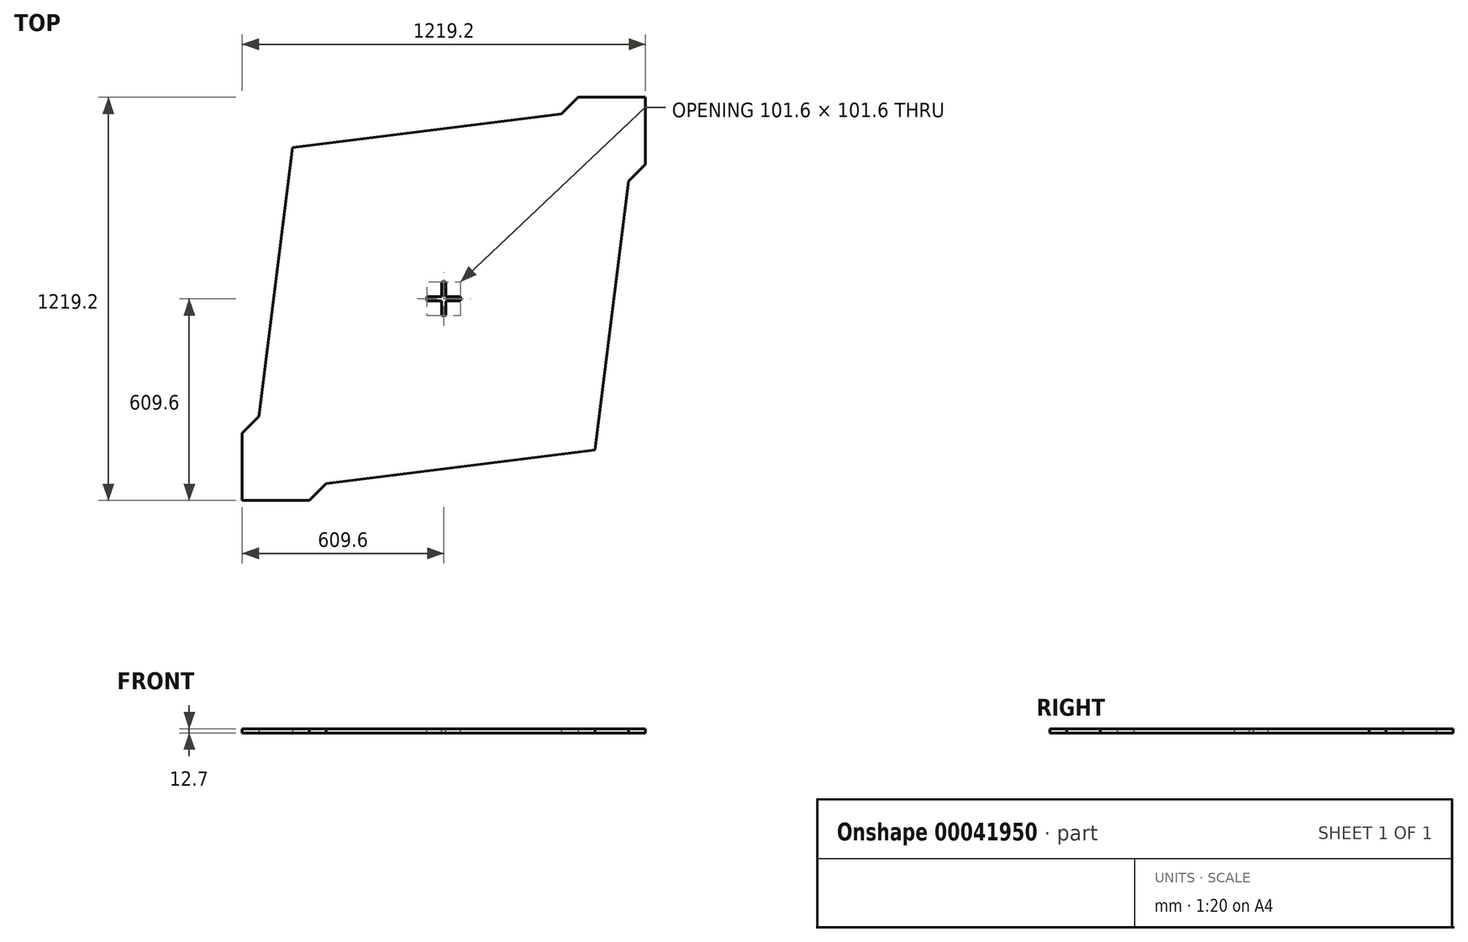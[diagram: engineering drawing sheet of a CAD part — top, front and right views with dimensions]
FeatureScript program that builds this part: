
annotation { "Feature Type Name" : "Feature", "Feature Type Description" : "" }
export const myFeature = defineFeature(function(context is Context, id is Id, definition is map)
    precondition{}
    {
        {
            var Q0;
            Q0=qCreatedBy(makeId("Top.planeOp"),FACE);
            var sketch = newSketch(context, id + "F0", { "sketchPlane" : qUnion([Q0])});
            skLineSegment(sketch, "E0.bottom", {"start": v(0, 0) * mm, "end": v(1219.2, 0) * mm});
            skLineSegment(sketch, "E0.top", {"start": v(0, 1219.2) * mm, "end": v(1219.2, 1219.2) * mm});
            skLineSegment(sketch, "E0.left", {"start": v(0, 0) * mm, "end": v(0, 1219.2) * mm});
            skLineSegment(sketch, "E0.right", {"start": v(1219.2, 0) * mm, "end": v(1219.2, 1219.2) * mm});
            skSolve(sketch);
        }
        {
            var Q0;
            Q0 = qSketchRegion(id + "F0", true);
            extrude(context, id + "F1", {"entities" : qUnion([Q0]), "depth" : 12.7 * mm});
        }
        {
            var Q0;
            Q0=makeQuery(id+"F1.opExtrude","CAP_FACE",FACE,{"disambiguationData":[OSD([sQuery(id+"F0.wireOp",EDGE,"E0.bottom"),sQuery(id+"F0.wireOp",EDGE,"E0.top"),sQuery(id+"F0.wireOp",EDGE,"E0.left"),sQuery(id+"F0.wireOp",EDGE,"E0.right")])],"isStart":true});
            var sketch = newSketch(context, id + "F2", { "sketchPlane" : qUnion([Q0])});
            skLineSegment(sketch, "E1", {"start": v(0, -203.2) * mm, "end": v(0, -1219.2) * mm});
            skLineSegment(sketch, "E2", {"start": v(0, -1219.2) * mm, "end": v(1016, -1219.2) * mm});
            skLineSegment(sketch, "E3", {"start": v(0, -203.2) * mm, "end": v(50.8, -254) * mm});
            skLineSegment(sketch, "E4", {"start": v(50.8, -254) * mm, "end": v(152.4, -1066.8) * mm});
            skLineSegment(sketch, "E5", {"start": v(152.4, -1066.8) * mm, "end": v(965.2, -1168.4) * mm});
            skLineSegment(sketch, "E6", {"start": v(1016, -1219.2) * mm, "end": v(965.2, -1168.4) * mm});
            skSolve(sketch);
        }
        {
            var Q0;
            Q0=makeQuery(id+"F2.imprint","IMPRINT",FACE,{"disambiguationData":[TD([[makeQuery(id+"F2.imprint","IMPRINT",EDGE,{"derivedFrom":sQuery(id+"F2.wireOp",EDGE,"E1")}),1.0]])]});
            extrude(context, id + "F3", {"entities" : qUnion([Q0]), "operationType" : NewBodyOperationType.REMOVE, "endBound" : BoundingType.THROUGH_ALL, "oppositeDirection" : true, "depth" : 25.4 * mm});
        }
        {
            var Q0;
            Q0=makeQuery(id+"F1.opExtrude","CAP_FACE",FACE,{"disambiguationData":[OSD([sQuery(id+"F0.wireOp",EDGE,"E0.bottom"),sQuery(id+"F0.wireOp",EDGE,"E0.top"),sQuery(id+"F0.wireOp",EDGE,"E0.left"),sQuery(id+"F0.wireOp",EDGE,"E0.right")])],"isStart":true});
            var sketch = newSketch(context, id + "F4", { "sketchPlane" : qUnion([Q0])});
            skLineSegment(sketch, "E7.MirrorCS", {"start": v(1066.8, -152.4) * mm, "end": v(1168.4, -965.2) * mm});
            skLineSegment(sketch, "E8.MirrorCS", {"start": v(254, -50.8) * mm, "end": v(1066.8, -152.4) * mm});
            skLineSegment(sketch, "E9.MirrorCS", {"start": v(1168.4, -965.2) * mm, "end": v(1219.2, -1016) * mm});
            skLineSegment(sketch, "E10.MirrorCS", {"start": v(203.2, 0) * mm, "end": v(254, -50.8) * mm});
            skLineSegment(sketch, "E11.MirrorCS", {"start": v(1219.2, 0) * mm, "end": v(203.2, 0) * mm});
            skLineSegment(sketch, "E12.MirrorCS", {"start": v(1219.2, -1016) * mm, "end": v(1219.2, 0) * mm});
            skSolve(sketch);
        }
        {
            var Q0;
            Q0 = qSketchRegion(id + "F4", true);
            extrude(context, id + "F5", {"entities" : qUnion([Q0]), "operationType" : NewBodyOperationType.REMOVE, "endBound" : BoundingType.THROUGH_ALL, "oppositeDirection" : true, "depth" : 25.4 * mm});
        }
        {
            var Q0;
            Q0=makeQuery(id+"F1.opExtrude","CAP_FACE",FACE,{"disambiguationData":[OSD([sQuery(id+"F0.wireOp",EDGE,"E0.bottom"),sQuery(id+"F0.wireOp",EDGE,"E0.top"),sQuery(id+"F0.wireOp",EDGE,"E0.left"),sQuery(id+"F0.wireOp",EDGE,"E0.right")])],"isStart":false});
            var sketch = newSketch(context, id + "F6", { "sketchPlane" : qUnion([Q0])});
            skLineSegment(sketch, "E13", {"start": v(609.6, 660.4) * mm, "end": v(609.6, 558.8) * mm});
            skLineSegment(sketch, "E14", {"start": v(558.8, 609.6) * mm, "end": v(660.4, 609.6) * mm});
            skLineSegment(sketch, "E15", {"start": v(609.6, 660.4) * mm, "end": v(615.95, 660.4) * mm});
            skLineSegment(sketch, "E16.MirrorCS", {"start": v(609.6, 660.4) * mm, "end": v(603.25, 660.4) * mm});
            skLineSegment(sketch, "E17.MirrorCS", {"start": v(609.6, 558.8) * mm, "end": v(603.25, 558.8) * mm});
            skLineSegment(sketch, "E18.MirrorCS", {"start": v(609.6, 558.8) * mm, "end": v(615.95, 558.8) * mm});
            skLineSegment(sketch, "E19", {"start": v(603.25, 660.4) * mm, "end": v(603.25, 558.8) * mm});
            skLineSegment(sketch, "E20", {"start": v(615.95, 660.4) * mm, "end": v(615.95, 558.8) * mm});
            skLineSegment(sketch, "E21", {"start": v(558.8, 609.6) * mm, "end": v(558.8, 615.95) * mm});
            skLineSegment(sketch, "E22.MirrorCS", {"start": v(660.4, 609.6) * mm, "end": v(660.4, 615.95) * mm});
            skLineSegment(sketch, "E23.MirrorCS", {"start": v(558.8, 609.6) * mm, "end": v(558.8, 603.25) * mm});
            skLineSegment(sketch, "E24.MirrorCS", {"start": v(660.4, 609.6) * mm, "end": v(660.4, 603.25) * mm});
            skLineSegment(sketch, "E25", {"start": v(558.8, 615.95) * mm, "end": v(660.4, 615.95) * mm});
            skLineSegment(sketch, "E26", {"start": v(660.4, 603.25) * mm, "end": v(558.8, 603.25) * mm});
            skSolve(sketch);
        }
        {
            var Q0;
            {var subQ3=sQuery(id+"F6.wireOp",EDGE,"E17.MirrorCS");Q0=makeQuery(id+"F6.imprint","IMPRINT",FACE,{"disambiguationData":[TD([[makeQuery(id+"F6.imprint","IMPRINT",EDGE,{"derivedFrom":subQ3}),-1.0]])]});}
            var Q1;
            {var subQ5=sQuery(id+"F6.wireOp",EDGE,"E18.MirrorCS");Q1=makeQuery(id+"F6.imprint","IMPRINT",FACE,{"disambiguationData":[TD([[makeQuery(id+"F6.imprint","IMPRINT",EDGE,{"derivedFrom":subQ5}),1.0]])]});}
            var Q2;
            {var subQ3=sQuery(id+"F6.wireOp",EDGE,"E21");Q2=makeQuery(id+"F6.imprint","IMPRINT",FACE,{"disambiguationData":[TD([[makeQuery(id+"F6.imprint","IMPRINT",EDGE,{"derivedFrom":subQ3}),-1.0]])]});}
            var Q3;
            {var subQ3=sQuery(id+"F6.wireOp",EDGE,"E23.MirrorCS");Q3=makeQuery(id+"F6.imprint","IMPRINT",FACE,{"disambiguationData":[TD([[makeQuery(id+"F6.imprint","IMPRINT",EDGE,{"derivedFrom":subQ3}),1.0]])]});}
            var Q4;
            {var subQ3=sQuery(id+"F6.wireOp",EDGE,"E22.MirrorCS");Q4=makeQuery(id+"F6.imprint","IMPRINT",FACE,{"disambiguationData":[TD([[makeQuery(id+"F6.imprint","IMPRINT",EDGE,{"derivedFrom":subQ3}),1.0]])]});}
            var Q5;
            {var subQ3=sQuery(id+"F6.wireOp",EDGE,"E24.MirrorCS");Q5=makeQuery(id+"F6.imprint","IMPRINT",FACE,{"disambiguationData":[TD([[makeQuery(id+"F6.imprint","IMPRINT",EDGE,{"derivedFrom":subQ3}),-1.0]])]});}
            var Q6;
            {var subQ1=sQuery(id+"F6.wireOp",EDGE,"E25");var subQ5=sQuery(id+"F6.wireOp",EDGE,"E13");var subQ6=makeQuery(id+"F6.imprint","INTERSECT",VERTEX,{"derivedFrom":[subQ5,subQ1]});Q6=makeQuery(id+"F6.imprint","IMPRINT",FACE,{"disambiguationData":[TD([[makeQuery(id+"F6.imprint","IMPRINT",EDGE,{"disambiguationData":[TD([[subQ6,-1.0]])],"derivedFrom":subQ5}),-1.0]])]});}
            var Q7;
            {var subQ0=sQuery(id+"F6.wireOp",EDGE,"E25");var subQ3=sQuery(id+"F6.wireOp",EDGE,"E13");var subQ4=makeQuery(id+"F6.imprint","INTERSECT",VERTEX,{"derivedFrom":[subQ3,subQ0]});Q7=makeQuery(id+"F6.imprint","IMPRINT",FACE,{"disambiguationData":[TD([[makeQuery(id+"F6.imprint","IMPRINT",EDGE,{"disambiguationData":[TD([[subQ4,-1.0]])],"derivedFrom":subQ3}),1.0]])]});}
            var Q8;
            {var subQ3=sQuery(id+"F6.wireOp",EDGE,"E13");var subQ5=sQuery(id+"F6.wireOp",EDGE,"E14");var subQ7=makeQuery(id+"F6.imprint","INTERSECT",VERTEX,{"derivedFrom":[subQ3,subQ5]});Q8=makeQuery(id+"F6.imprint","IMPRINT",FACE,{"disambiguationData":[TD([[makeQuery(id+"F6.imprint","IMPRINT",EDGE,{"disambiguationData":[TD([[subQ7,-1.0]])],"derivedFrom":subQ3}),-1.0]])]});}
            var Q9;
            {var subQ3=sQuery(id+"F6.wireOp",EDGE,"E13");var subQ5=sQuery(id+"F6.wireOp",EDGE,"E14");var subQ7=makeQuery(id+"F6.imprint","INTERSECT",VERTEX,{"derivedFrom":[subQ3,subQ5]});Q9=makeQuery(id+"F6.imprint","IMPRINT",FACE,{"disambiguationData":[TD([[makeQuery(id+"F6.imprint","IMPRINT",EDGE,{"disambiguationData":[TD([[subQ7,-1.0]])],"derivedFrom":subQ3}),1.0]])]});}
            var Q10;
            {var subQ5=sQuery(id+"F6.wireOp",EDGE,"E16.MirrorCS");Q10=makeQuery(id+"F6.imprint","IMPRINT",FACE,{"disambiguationData":[TD([[makeQuery(id+"F6.imprint","IMPRINT",EDGE,{"derivedFrom":subQ5}),1.0]])]});}
            var Q11;
            {var subQ0=sQuery(id+"F6.wireOp",EDGE,"E15");Q11=makeQuery(id+"F6.imprint","IMPRINT",FACE,{"disambiguationData":[TD([[makeQuery(id+"F6.imprint","IMPRINT",EDGE,{"derivedFrom":subQ0}),-1.0]])]});}
            extrude(context, id + "F7", {"entities" : qUnion([Q0, Q1, Q2, Q3, Q4, Q5, Q6, Q7, Q8, Q9, Q10, Q11]), "operationType" : NewBodyOperationType.REMOVE, "endBound" : BoundingType.THROUGH_ALL, "oppositeDirection" : true, "depth" : 25.4 * mm});
        }
    });
